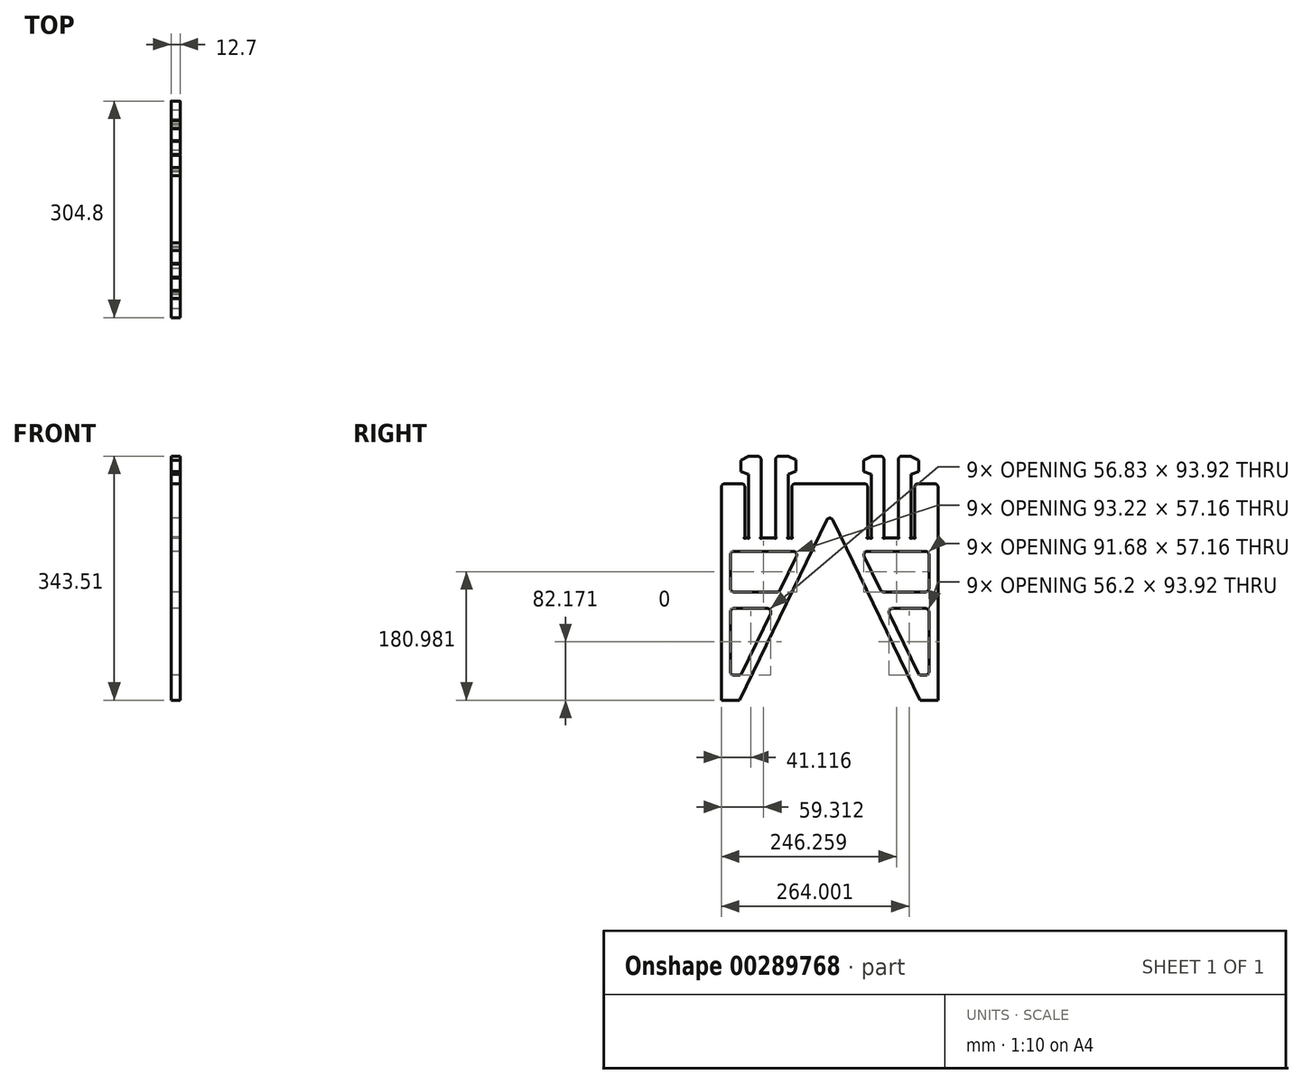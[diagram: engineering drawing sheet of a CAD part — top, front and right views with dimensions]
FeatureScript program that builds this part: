
annotation { "Feature Type Name" : "Feature", "Feature Type Description" : "" }
export const myFeature = defineFeature(function(context is Context, id is Id, definition is map)
    precondition{}
    {
        {
            var Q0;
            Q0=qCreatedBy(makeId("Right.planeOp"),FACE);
            var sketch = newSketch(context, id + "F0", { "sketchPlane" : qUnion([Q0])});
            skLineSegment(sketch, "E0.bottom", {"start": v(152.4, 152.4) * mm, "end": v(-152.4, 152.4) * mm});
            skLineSegment(sketch, "E0.top", {"start": v(152.4, -152.4) * mm, "end": v(-152.4, -152.4) * mm});
            skLineSegment(sketch, "E0.left", {"start": v(152.4, 152.4) * mm, "end": v(152.4, -152.4) * mm});
            skLineSegment(sketch, "E0.right", {"start": v(-152.4, 152.4) * mm, "end": v(-152.4, -152.4) * mm});
            skPoint(sketch, "E0.middle", {"position": v(0, 0) * mm});
            skLineSegment(sketch, "E1", {"start": v(20.32, 152.4) * mm, "end": v(-127, -152.4) * mm});
            skLineSegment(sketch, "E2", {"start": v(-20.32, 152.4) * mm, "end": v(127, -152.4) * mm});
            skLineSegment(sketch, "E3", {"start": v(-76.2, 152.4) * mm, "end": v(-76.2, 76.2) * mm});
            skLineSegment(sketch, "E4", {"start": v(-76.2, 76.2) * mm, "end": v(-96.52, 76.2) * mm});
            skLineSegment(sketch, "E5", {"start": v(-96.52, 76.2) * mm, "end": v(-96.52, 152.4) * mm});
            skLineSegment(sketch, "E6", {"start": v(-114.3, 165.6) * mm, "end": v(-114.3, 76.2) * mm});
            skLineSegment(sketch, "E7", {"start": v(-153.35, 165.6) * mm, "end": v(152.08, 165.6) * mm, "construction": true});
            skLineSegment(sketch, "E8", {"start": v(-155.47, 191) * mm, "end": v(152.66, 191) * mm, "construction": true});
            skLineSegment(sketch, "E9", {"start": v(-96.52, 152.4) * mm, "end": v(-96.52, 191) * mm});
            skLineSegment(sketch, "E10", {"start": v(-96.52, 191) * mm, "end": v(-114.49, 191) * mm});
            skLineSegment(sketch, "E11", {"start": v(-114.49, 191) * mm, "end": v(-125.17, 185.46) * mm});
            skLineSegment(sketch, "E12", {"start": v(-125.17, 185.46) * mm, "end": v(-125.17, 169.5) * mm});
            skLineSegment(sketch, "E13", {"start": v(-125.17, 169.5) * mm, "end": v(-113.72, 165.4) * mm});
            skLineSegment(sketch, "E14", {"start": v(-76.2, 152.4) * mm, "end": v(-76.2, 191) * mm});
            skLineSegment(sketch, "E15", {"start": v(-76.2, 191) * mm, "end": v(-58.23, 191) * mm});
            skLineSegment(sketch, "E16", {"start": v(-58.23, 191) * mm, "end": v(-47.24, 186.1) * mm});
            skLineSegment(sketch, "E17", {"start": v(-47.24, 186.1) * mm, "end": v(-47.24, 170.14) * mm});
            skLineSegment(sketch, "E18", {"start": v(-47.24, 170.14) * mm, "end": v(-58.42, 165.37) * mm});
            skLineSegment(sketch, "E19", {"start": v(-58.42, 165.37) * mm, "end": v(-58.42, 76.18) * mm});
            skLineSegment(sketch, "E20", {"start": v(-58.42, 76.2) * mm, "end": v(-53.34, 76.2) * mm});
            skLineSegment(sketch, "E21", {"start": v(-53.34, 76.2) * mm, "end": v(-53.34, 152.4) * mm});
            skLineSegment(sketch, "E22", {"start": v(-114.3, 76.2) * mm, "end": v(-119.38, 76.2) * mm});
            skLineSegment(sketch, "E23", {"start": v(-119.38, 76.2) * mm, "end": v(-119.38, 152.4) * mm});
            skLineSegment(sketch, "E24", {"start": v(96.52, 166.1) * mm, "end": v(96.52, 76.2) * mm});
            skLineSegment(sketch, "E25", {"start": v(96.52, 76.2) * mm, "end": v(76.2, 76.2) * mm});
            skLineSegment(sketch, "E26", {"start": v(76.2, 76.2) * mm, "end": v(76.2, 166.1) * mm});
            skLineSegment(sketch, "E27", {"start": v(58.42, 165.6) * mm, "end": v(58.42, 76.2) * mm});
            skLineSegment(sketch, "E28", {"start": v(76.2, 166.1) * mm, "end": v(76.2, 191.15) * mm});
            skLineSegment(sketch, "E29", {"start": v(76.2, 191.15) * mm, "end": v(59.04, 191) * mm});
            skLineSegment(sketch, "E30", {"start": v(59.04, 191) * mm, "end": v(47.55, 185.42) * mm});
            skLineSegment(sketch, "E31", {"start": v(47.55, 185.42) * mm, "end": v(47.55, 169.46) * mm});
            skLineSegment(sketch, "E32", {"start": v(47.55, 169.46) * mm, "end": v(58.42, 165.6) * mm});
            skLineSegment(sketch, "E33", {"start": v(96.52, 166.1) * mm, "end": v(96.52, 191.14) * mm});
            skLineSegment(sketch, "E34", {"start": v(96.52, 191.14) * mm, "end": v(113.69, 191) * mm});
            skLineSegment(sketch, "E35", {"start": v(113.69, 191) * mm, "end": v(125.17, 185.42) * mm});
            skLineSegment(sketch, "E36", {"start": v(125.17, 185.42) * mm, "end": v(125.17, 169.46) * mm});
            skLineSegment(sketch, "E37", {"start": v(125.17, 169.46) * mm, "end": v(114.3, 165.6) * mm});
            skLineSegment(sketch, "E38", {"start": v(114.3, 165.6) * mm, "end": v(114.3, 76.2) * mm});
            skLineSegment(sketch, "E39", {"start": v(114.3, 76.2) * mm, "end": v(119.38, 76.2) * mm});
            skLineSegment(sketch, "E40", {"start": v(58.42, 76.2) * mm, "end": v(53.34, 76.2) * mm});
            skLineSegment(sketch, "E41", {"start": v(53.34, 76.2) * mm, "end": v(53.34, 152.4) * mm});
            skLineSegment(sketch, "E42", {"start": v(119.38, 76.2) * mm, "end": v(119.38, 152.4) * mm});
            skLineSegment(sketch, "E43", {"start": v(-139.7, -117.2) * mm, "end": v(-139.7, -23.27) * mm});
            skLineSegment(sketch, "E44", {"start": v(-139.7, -23.27) * mm, "end": v(-79.84, -23.27) * mm});
            skLineSegment(sketch, "E45", {"start": v(-139.7, 0) * mm, "end": v(-139.7, 57.16) * mm});
            skLineSegment(sketch, "E46", {"start": v(-139.7, 57.16) * mm, "end": v(-43.45, 57.16) * mm});
            skLineSegment(sketch, "E47", {"start": v(-139.7, 0) * mm, "end": v(-71.08, 0) * mm});
            skPoint(sketch, "E47.endSnap0", {"position": v(-53.34, 0) * mm});
            skLineSegment(sketch, "E48", {"start": v(-71.08, 0) * mm, "end": v(-43.45, 57.16) * mm});
            skLineSegment(sketch, "E49", {"start": v(-79.84, -23.27) * mm, "end": v(-125.24, -117.2) * mm});
            skLineSegment(sketch, "E50", {"start": v(-125.24, -117.2) * mm, "end": v(-139.7, -117.2) * mm});
            skLineSegment(sketch, "E51", {"start": v(72.62, 0) * mm, "end": v(45, 57.16) * mm});
            skLineSegment(sketch, "E52", {"start": v(45, 57.16) * mm, "end": v(139.7, 57.16) * mm});
            skLineSegment(sketch, "E53", {"start": v(72.62, 0) * mm, "end": v(139.7, 0) * mm});
            skPoint(sketch, "E53.endSnap0", {"position": v(-0.59, 0) * mm});
            skLineSegment(sketch, "E54", {"start": v(139.7, 0) * mm, "end": v(139.7, 57.16) * mm});
            skLineSegment(sketch, "E55", {"start": v(125.87, -117.2) * mm, "end": v(80.48, -23.27) * mm});
            skLineSegment(sketch, "E56", {"start": v(80.48, -23.27) * mm, "end": v(139.7, -23.27) * mm});
            skLineSegment(sketch, "E57", {"start": v(139.7, -23.27) * mm, "end": v(139.7, -117.2) * mm});
            skLineSegment(sketch, "E58", {"start": v(139.7, -117.2) * mm, "end": v(125.87, -117.2) * mm});
            skLineSegment(sketch, "E59", {"start": v(-152.4, -23.27) * mm, "end": v(152.4, -23.27) * mm, "construction": true});
            skLineSegment(sketch, "E60", {"start": v(-152.4, -117.2) * mm, "end": v(152.4, -117.2) * mm, "construction": true});
            skPoint(sketch, "E60.startSnap0", {"position": v(-132.47, -117.2) * mm});
            skLineSegment(sketch, "E61", {"start": v(-152.4, 57.16) * mm, "end": v(152.4, 57.16) * mm, "construction": true});
            skLineSegment(sketch, "E62", {"start": v(-152.4, 0) * mm, "end": v(152.4, 0) * mm, "construction": true});
            skLineSegment(sketch, "E63", {"start": v(-139.7, 42.44) * mm, "end": v(-139.7, -70.23) * mm, "construction": true});
            skLineSegment(sketch, "E64.MirrorCS", {"start": v(139.7, 42.44) * mm, "end": v(139.7, -70.23) * mm, "construction": true});
            skArc(sketch, "E65", {"start": v(-119.38, 77.21) * mm, "mid": v(-120.1, 75.49) * mm, "end": v(-118.37, 76.2) * mm});
            skArc(sketch, "E66", {"start": v(-114.3, 77.2) * mm, "mid": v(-113.59, 75.49) * mm, "end": v(-115.3, 76.2) * mm});
            skArc(sketch, "E67", {"start": v(-96.52, 77.23) * mm, "mid": v(-97.25, 75.47) * mm, "end": v(-95.5, 76.2) * mm});
            skArc(sketch, "E68", {"start": v(-76.2, 77.22) * mm, "mid": v(-75.48, 75.48) * mm, "end": v(-77.22, 76.2) * mm});
            skArc(sketch, "E69", {"start": v(-58.42, 77.2) * mm, "mid": v(-59.13, 75.46) * mm, "end": v(-57.4, 76.2) * mm});
            skArc(sketch, "E70", {"start": v(-54.36, 76.2) * mm, "mid": v(-52.62, 75.48) * mm, "end": v(-53.34, 77.22) * mm});
            skArc(sketch, "E71.MirrorCS", {"start": v(119.38, 77.21) * mm, "mid": v(120.1, 75.49) * mm, "end": v(118.37, 76.2) * mm});
            skArc(sketch, "E72.MirrorCS", {"start": v(114.3, 77.2) * mm, "mid": v(113.59, 75.49) * mm, "end": v(115.3, 76.2) * mm});
            skArc(sketch, "E73.MirrorCS", {"start": v(96.52, 77.23) * mm, "mid": v(97.25, 75.47) * mm, "end": v(95.5, 76.2) * mm});
            skArc(sketch, "E74.MirrorCS", {"start": v(76.2, 77.22) * mm, "mid": v(75.48, 75.48) * mm, "end": v(77.22, 76.2) * mm});
            skArc(sketch, "E75.MirrorCS", {"start": v(58.42, 77.2) * mm, "mid": v(59.13, 75.46) * mm, "end": v(57.4, 76.2) * mm});
            skLineSegment(sketch, "E76", {"start": v(-58.42, 76.18) * mm, "end": v(-58.42, 76.2) * mm});
            skArc(sketch, "E77.MirrorCS", {"start": v(54.36, 76.2) * mm, "mid": v(52.62, 75.48) * mm, "end": v(53.34, 77.22) * mm});
            skSolve(sketch);
        }
        {
            var Q0;
            {var subQ10=sQuery(id+"F0.wireOp",EDGE,"E0.right");Q0=makeQuery(id+"F0.imprint","IMPRINT",FACE,{"disambiguationData":[TD([[makeQuery(id+"F0.imprint","IMPRINT",EDGE,{"derivedFrom":subQ10}),1.0]])]});}
            var Q1;
            {var subQ0=sQuery(id+"F0.wireOp",EDGE,"E1");var subQ1=sQuery(id+"F0.wireOp",EDGE,"E0.bottom");var subQ2=makeQuery(id+"F0.imprint","INTERSECT",VERTEX,{"derivedFrom":[subQ1,subQ0]});Q1=makeQuery(id+"F0.imprint","IMPRINT",FACE,{"disambiguationData":[TD([[makeQuery(id+"F0.imprint","IMPRINT",EDGE,{"disambiguationData":[TD([[subQ2,-1.0]])],"derivedFrom":subQ1}),1.0]])]});}
            var Q2;
            {var subQ0=sQuery(id+"F0.wireOp",EDGE,"E9");Q2=makeQuery(id+"F0.imprint","IMPRINT",FACE,{"disambiguationData":[TD([[makeQuery(id+"F0.imprint","IMPRINT",EDGE,{"derivedFrom":subQ0}),1.0]])]});}
            var Q3;
            {var subQ0=sQuery(id+"F0.wireOp",EDGE,"E14");Q3=makeQuery(id+"F0.imprint","IMPRINT",FACE,{"disambiguationData":[TD([[makeQuery(id+"F0.imprint","IMPRINT",EDGE,{"derivedFrom":subQ0}),-1.0]])]});}
            var Q4;
            {var subQ7=sQuery(id+"F0.wireOp",EDGE,"E0.left");Q4=makeQuery(id+"F0.imprint","IMPRINT",FACE,{"disambiguationData":[TD([[makeQuery(id+"F0.imprint","IMPRINT",EDGE,{"derivedFrom":subQ7}),-1.0]])]});}
            var Q5;
            {var subQ0=sQuery(id+"F0.wireOp",EDGE,"E28");Q5=makeQuery(id+"F0.imprint","IMPRINT",FACE,{"disambiguationData":[TD([[makeQuery(id+"F0.imprint","IMPRINT",EDGE,{"derivedFrom":subQ0}),1.0]])]});}
            var Q6;
            {var subQ0=sQuery(id+"F0.wireOp",EDGE,"E33");Q6=makeQuery(id+"F0.imprint","IMPRINT",FACE,{"disambiguationData":[TD([[makeQuery(id+"F0.imprint","IMPRINT",EDGE,{"derivedFrom":subQ0}),-1.0]])]});}
            extrude(context, id + "F1", {"entities" : qUnion([Q0, Q1, Q2, Q3, Q4, Q5, Q6]), "depth" : 12.7 * mm});
        }
        {
            var Q0;
            Q0=makeQuery(id+"F1.opExtrude","SWEPT_EDGE",EDGE,{"disambiguationData":[OSD([sQuery(id+"F0.wireOp",EDGE,"E45"),sQuery(id+"F0.wireOp",EDGE,"E46")])]});
            var Q1;
            Q1=makeQuery(id+"F1.opExtrude","SWEPT_EDGE",EDGE,{"disambiguationData":[OSD([sQuery(id+"F0.wireOp",EDGE,"E46"),sQuery(id+"F0.wireOp",EDGE,"E48")])]});
            var Q2;
            Q2=makeQuery(id+"F1.opExtrude","SWEPT_EDGE",EDGE,{"disambiguationData":[OSD([sQuery(id+"F0.wireOp",EDGE,"E47"),sQuery(id+"F0.wireOp",EDGE,"E48")])]});
            var Q3;
            Q3=makeQuery(id+"F1.opExtrude","SWEPT_EDGE",EDGE,{"disambiguationData":[OSD([sQuery(id+"F0.wireOp",EDGE,"E45"),sQuery(id+"F0.wireOp",EDGE,"E47")])]});
            fillet(context, id + "F2", {"entities" : qUnion([Q0, Q1, Q2, Q3]), "radius" : 5.08 * mm, "tangentPropagation" : true, "allowEdgeOverflow" : false});
        }
        {
            var Q0;
            Q0=makeQuery(id+"F1.opExtrude","SWEPT_EDGE",EDGE,{"disambiguationData":[OSD([sQuery(id+"F0.wireOp",EDGE,"E43"),sQuery(id+"F0.wireOp",EDGE,"E44")])]});
            var Q1;
            Q1=makeQuery(id+"F1.opExtrude","SWEPT_EDGE",EDGE,{"disambiguationData":[OSD([sQuery(id+"F0.wireOp",EDGE,"E44"),sQuery(id+"F0.wireOp",EDGE,"E49")])]});
            var Q2;
            Q2=makeQuery(id+"F1.opExtrude","SWEPT_EDGE",EDGE,{"disambiguationData":[OSD([sQuery(id+"F0.wireOp",EDGE,"E49"),sQuery(id+"F0.wireOp",EDGE,"E50")])]});
            var Q3;
            Q3=makeQuery(id+"F1.opExtrude","SWEPT_EDGE",EDGE,{"disambiguationData":[OSD([sQuery(id+"F0.wireOp",EDGE,"E43"),sQuery(id+"F0.wireOp",EDGE,"E50")])]});
            fillet(context, id + "F3", {"entities" : qUnion([Q0, Q1, Q2, Q3]), "radius" : 5.08 * mm, "tangentPropagation" : true, "allowEdgeOverflow" : false});
        }
        {
            var Q0;
            Q0=makeQuery(id+"F1.opExtrude","SWEPT_EDGE",EDGE,{"disambiguationData":[OSD([sQuery(id+"F0.wireOp",EDGE,"E52"),sQuery(id+"F0.wireOp",EDGE,"E54")])]});
            var Q1;
            Q1=makeQuery(id+"F1.opExtrude","SWEPT_EDGE",EDGE,{"disambiguationData":[OSD([sQuery(id+"F0.wireOp",EDGE,"E51"),sQuery(id+"F0.wireOp",EDGE,"E52")])]});
            var Q2;
            Q2=makeQuery(id+"F1.opExtrude","SWEPT_EDGE",EDGE,{"disambiguationData":[OSD([sQuery(id+"F0.wireOp",EDGE,"E51"),sQuery(id+"F0.wireOp",EDGE,"E53")])]});
            var Q3;
            Q3=makeQuery(id+"F1.opExtrude","SWEPT_EDGE",EDGE,{"disambiguationData":[OSD([sQuery(id+"F0.wireOp",EDGE,"E53"),sQuery(id+"F0.wireOp",EDGE,"E54")])]});
            var Q4;
            Q4=makeQuery(id+"F1.opExtrude","SWEPT_EDGE",EDGE,{"disambiguationData":[OSD([sQuery(id+"F0.wireOp",EDGE,"E56"),sQuery(id+"F0.wireOp",EDGE,"E57")])]});
            var Q5;
            Q5=makeQuery(id+"F1.opExtrude","SWEPT_EDGE",EDGE,{"disambiguationData":[OSD([sQuery(id+"F0.wireOp",EDGE,"E55"),sQuery(id+"F0.wireOp",EDGE,"E56")])]});
            var Q6;
            Q6=makeQuery(id+"F1.opExtrude","SWEPT_EDGE",EDGE,{"disambiguationData":[OSD([sQuery(id+"F0.wireOp",EDGE,"E55"),sQuery(id+"F0.wireOp",EDGE,"E58")])]});
            var Q7;
            Q7=makeQuery(id+"F1.opExtrude","SWEPT_EDGE",EDGE,{"disambiguationData":[OSD([sQuery(id+"F0.wireOp",EDGE,"E57"),sQuery(id+"F0.wireOp",EDGE,"E58")])]});
            fillet(context, id + "F4", {"entities" : qUnion([Q0, Q1, Q2, Q3, Q4, Q5, Q6, Q7]), "radius" : 5.08 * mm, "tangentPropagation" : true, "allowEdgeOverflow" : false});
        }
        {
            var Q0;
            Q0=makeQuery(id+"F1.opExtrude","SWEPT_EDGE",EDGE,{"disambiguationData":[OSD([sQuery(id+"F0.wireOp",EDGE,"E0.bottom"),sQuery(id+"F0.wireOp",EDGE,"E23")])]});
            var Q1;
            Q1=makeQuery(id+"F1.opExtrude","SWEPT_EDGE",EDGE,{"disambiguationData":[OSD([sQuery(id+"F0.wireOp",EDGE,"E0.bottom"),sQuery(id+"F0.wireOp",EDGE,"E0.right")])]});
            var Q2;
            Q2=makeQuery(id+"F1.opExtrude","SWEPT_EDGE",EDGE,{"disambiguationData":[OSD([sQuery(id+"F0.wireOp",EDGE,"E0.bottom"),sQuery(id+"F0.wireOp",EDGE,"E21")])]});
            var Q3;
            Q3=makeQuery(id+"F1.opExtrude","SWEPT_EDGE",EDGE,{"disambiguationData":[OSD([sQuery(id+"F0.wireOp",EDGE,"E0.bottom"),sQuery(id+"F0.wireOp",EDGE,"E41")])]});
            var Q4;
            Q4=makeQuery(id+"F1.opExtrude","SWEPT_EDGE",EDGE,{"disambiguationData":[OSD([sQuery(id+"F0.wireOp",EDGE,"E0.bottom"),sQuery(id+"F0.wireOp",EDGE,"E42")])]});
            var Q5;
            Q5=makeQuery(id+"F1.opExtrude","SWEPT_EDGE",EDGE,{"disambiguationData":[OSD([sQuery(id+"F0.wireOp",EDGE,"E0.bottom"),sQuery(id+"F0.wireOp",EDGE,"E0.left")])]});
            var Q6;
            Q6=makeQuery(id+"F1.opExtrude","SWEPT_EDGE",EDGE,{"disambiguationData":[OSD([sQuery(id+"F0.wireOp",EDGE,"E1"),sQuery(id+"F0.wireOp",EDGE,"E2")])]});
            var Q7;
            Q7=makeQuery(id+"F1.opExtrude","SWEPT_EDGE",EDGE,{"disambiguationData":[OSD([sQuery(id+"F0.wireOp",EDGE,"E9"),sQuery(id+"F0.wireOp",EDGE,"E10")])]});
            var Q8;
            Q8=makeQuery(id+"F1.opExtrude","SWEPT_EDGE",EDGE,{"disambiguationData":[OSD([sQuery(id+"F0.wireOp",EDGE,"E14"),sQuery(id+"F0.wireOp",EDGE,"E15")])]});
            var Q9;
            Q9=makeQuery(id+"F1.opExtrude","SWEPT_EDGE",EDGE,{"disambiguationData":[OSD([sQuery(id+"F0.wireOp",EDGE,"E33"),sQuery(id+"F0.wireOp",EDGE,"E34")])]});
            var Q10;
            Q10=makeQuery(id+"F1.opExtrude","SWEPT_EDGE",EDGE,{"disambiguationData":[OSD([sQuery(id+"F0.wireOp",EDGE,"E28"),sQuery(id+"F0.wireOp",EDGE,"E29")])]});
            fillet(context, id + "F5", {"entities" : qUnion([Q0, Q1, Q2, Q3, Q4, Q5, Q6, Q7, Q8, Q9, Q10]), "radius" : 5.08 * mm, "tangentPropagation" : true, "allowEdgeOverflow" : false});
        }
    });
